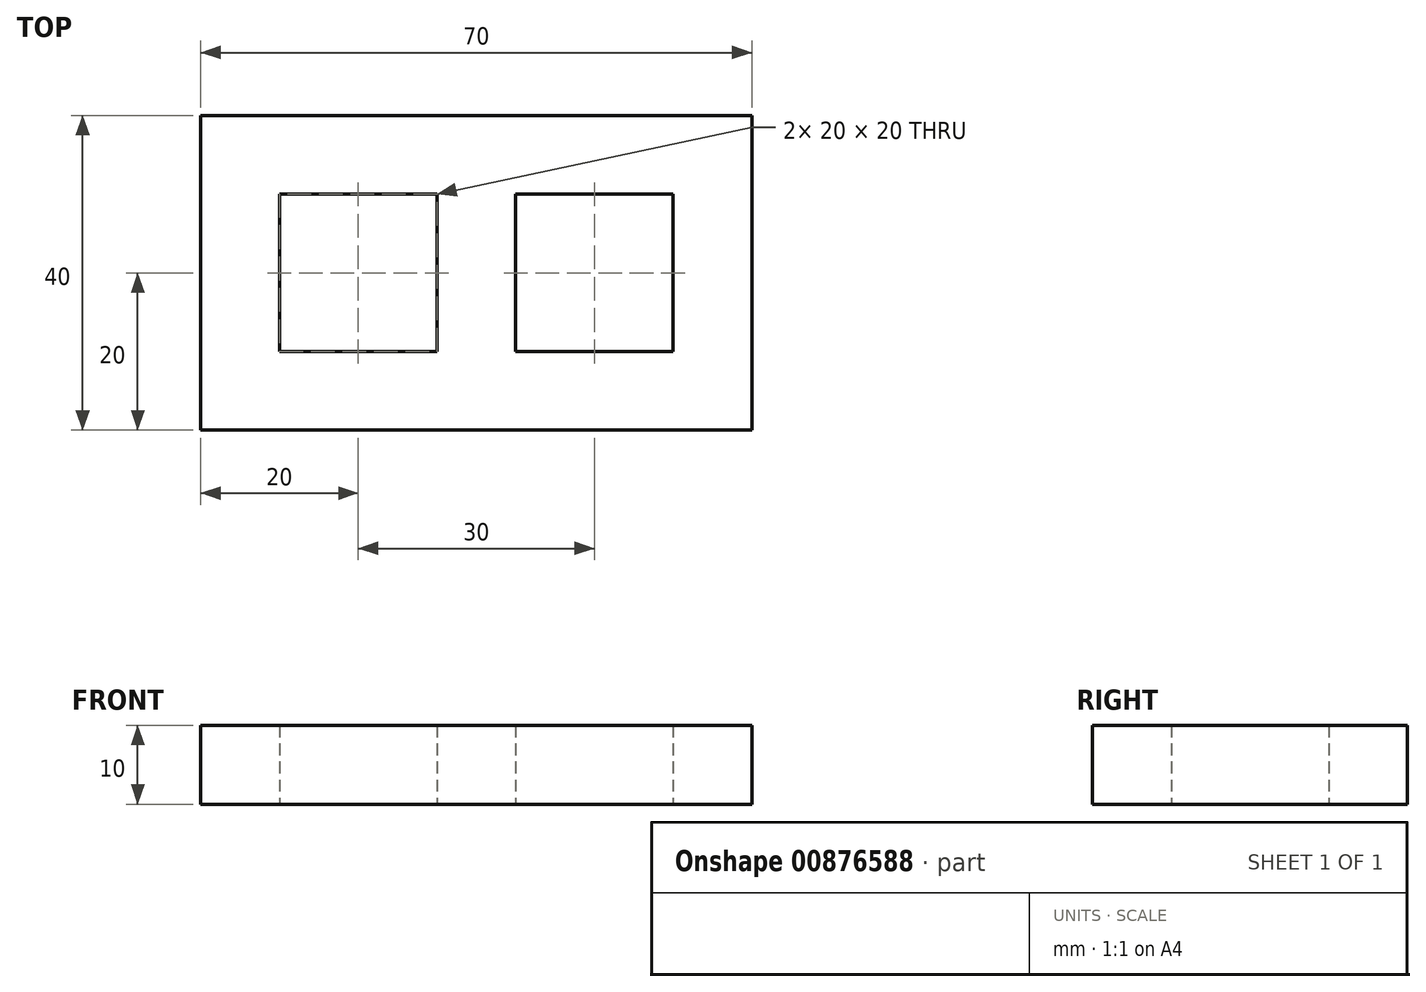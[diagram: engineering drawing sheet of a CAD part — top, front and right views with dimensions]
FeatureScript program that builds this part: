
annotation { "Feature Type Name" : "Feature", "Feature Type Description" : "" }
export const myFeature = defineFeature(function(context is Context, id is Id, definition is map)
    precondition{}
    {
        {
            var Q0;
            Q0=qCreatedBy(makeId("Top.planeOp"),FACE);
            var sketch = newSketch(context, id + "F0", { "sketchPlane" : qUnion([Q0])});
            skLineSegment(sketch, "E0.bottom", {"start": v(0, 0) * mm, "end": v(70, 0) * mm});
            skLineSegment(sketch, "E0.top", {"start": v(0, 40) * mm, "end": v(70, 40) * mm});
            skLineSegment(sketch, "E0.left", {"start": v(0, 0) * mm, "end": v(0, 40) * mm});
            skLineSegment(sketch, "E0.right", {"start": v(70, 0) * mm, "end": v(70, 40) * mm});
            skLineSegment(sketch, "E1", {"start": v(0, 40) * mm, "end": v(10, 40) * mm});
            skLineSegment(sketch, "E2", {"start": v(10, 40) * mm, "end": v(10, 30) * mm});
            skLineSegment(sketch, "E3.bottom", {"start": v(10, 30) * mm, "end": v(30, 30) * mm});
            skLineSegment(sketch, "E3.top", {"start": v(10, 10) * mm, "end": v(30, 10) * mm});
            skLineSegment(sketch, "E3.left", {"start": v(10, 30) * mm, "end": v(10, 10) * mm});
            skLineSegment(sketch, "E3.right", {"start": v(30, 30) * mm, "end": v(30, 10) * mm});
            skLineSegment(sketch, "E4", {"start": v(70, 40) * mm, "end": v(60, 40) * mm});
            skLineSegment(sketch, "E5", {"start": v(60, 40) * mm, "end": v(60, 30) * mm});
            skLineSegment(sketch, "E6.bottom", {"start": v(60, 30) * mm, "end": v(40, 30) * mm});
            skLineSegment(sketch, "E6.top", {"start": v(60, 10) * mm, "end": v(40, 10) * mm});
            skLineSegment(sketch, "E6.left", {"start": v(60, 30) * mm, "end": v(60, 10) * mm});
            skLineSegment(sketch, "E6.right", {"start": v(40, 30) * mm, "end": v(40, 10) * mm});
            skSolve(sketch);
        }
        {
            var Q0;
            Q0=makeQuery(id+"F0.imprint","IMPRINT",FACE,{"disambiguationData":[TD([[makeQuery(id+"F0.imprint","IMPRINT",EDGE,{"derivedFrom":sQuery(id+"F0.wireOp",EDGE,"E0.bottom")}),1.0]])]});
            extrude(context, id + "F1", {"entities" : qUnion([Q0]), "depth" : 10 * mm, "offsetDistance" : 25 * mm});
        }
    });
